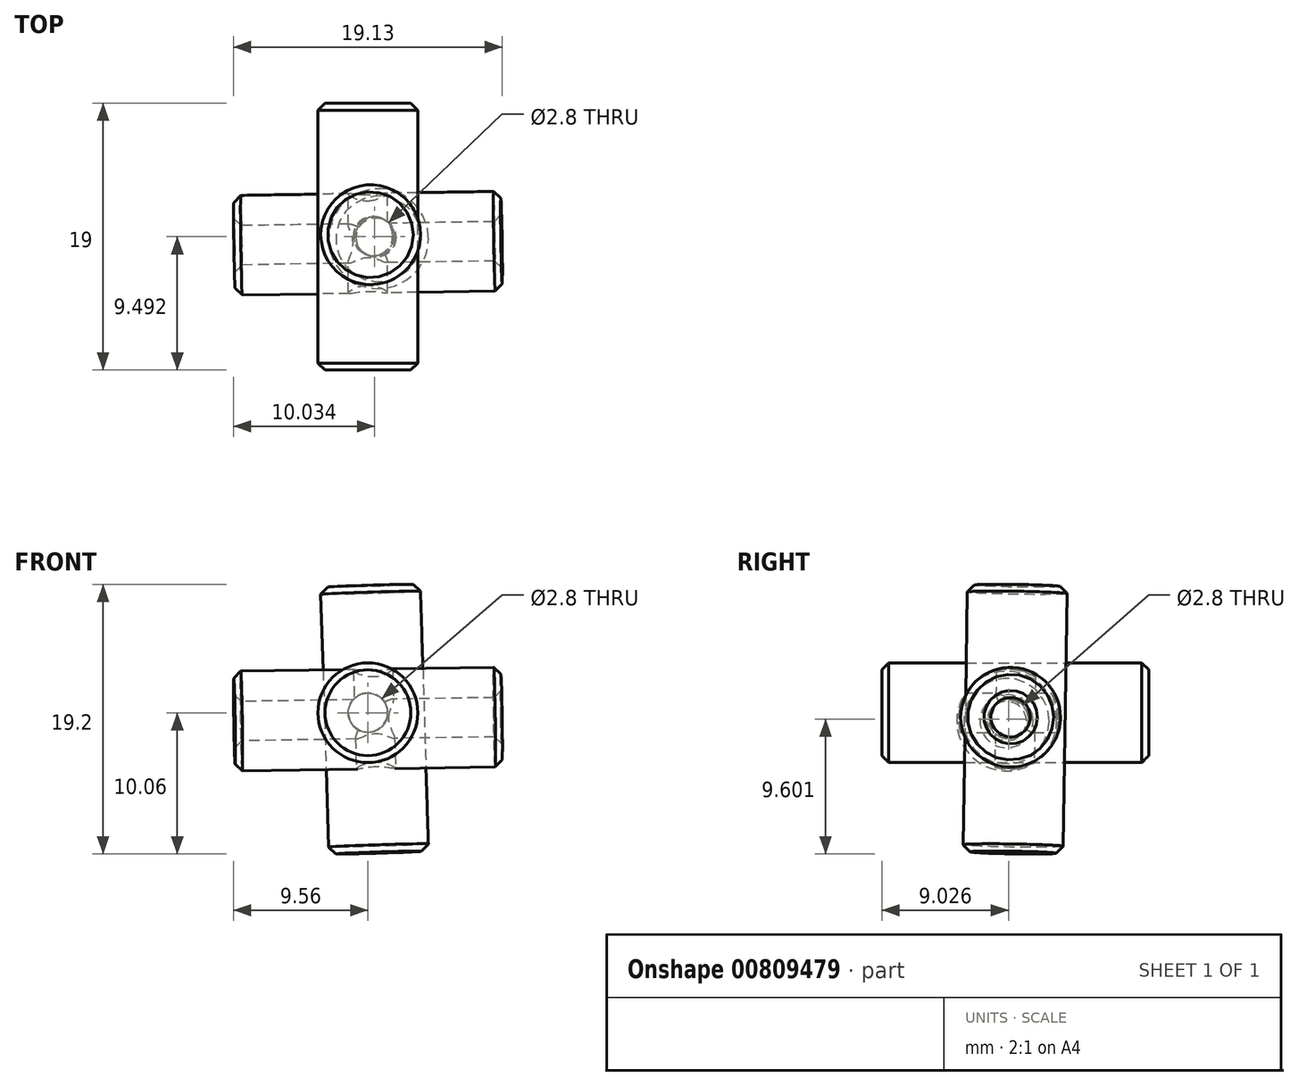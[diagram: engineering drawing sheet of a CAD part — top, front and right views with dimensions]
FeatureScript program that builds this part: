
annotation { "Feature Type Name" : "Feature", "Feature Type Description" : "" }
export const myFeature = defineFeature(function(context is Context, id is Id, definition is map)
    precondition{}
    {
        {
            var Q0;
            Q0=qCreatedBy(makeId("Front.planeOp"),FACE);
            var sketch = newSketch(context, id + "F0", { "sketchPlane" : qUnion([Q0])});
            skCircle(sketch, "E0", {"center": v(0, 0) * mm, "radius": 3.55 * mm});
            skSolve(sketch);
        }
        {
            var Q0;
            Q0=makeQuery(id+"F0.imprint","IMPRINT",FACE,{"disambiguationData":[TD([[makeQuery(id+"F0.imprint","IMPRINT",EDGE,{"derivedFrom":sQuery(id+"F0.wireOp",EDGE,"E0")}),1.0]])]});
            extrude(context, id + "F1", {"entities" : qUnion([Q0]), "endBound" : BoundingType.SYMMETRIC, "depth" : 19 * mm, "offsetDistance" : 25 * mm});
        }
        {
            var Q0;
            Q0=qCreatedBy(makeId("Front.planeOp"),FACE);
            var sketch = newSketch(context, id + "F2", { "sketchPlane" : qUnion([Q0])});
            skCircle(sketch, "E1", {"center": v(0, 0) * mm, "radius": 1.4 * mm});
            skSolve(sketch);
        }
        {
            var Q0;
            Q0 = qSketchRegion(id + "F2", true);
            extrude(context, id + "F3", {"entities" : qUnion([Q0]), "endBound" : BoundingType.SYMMETRIC, "depth" : 20 * mm, "offsetDistance" : 25 * mm});
        }
        {
            var Q0;
            Q0=qCreatedBy(makeId("Front.planeOp"),FACE);
            var sketch = newSketch(context, id + "F4", { "sketchPlane" : qUnion([Q0])});
            skLineSegment(sketch, "E2.bottom", {"start": v(0, 0) * mm, "end": v(10, 0) * mm});
            skLineSegment(sketch, "E2.top", {"start": v(0, 10) * mm, "end": v(10, 10) * mm});
            skLineSegment(sketch, "E2.left", {"start": v(0, 0) * mm, "end": v(0, 10) * mm});
            skLineSegment(sketch, "E2.right", {"start": v(10, 0) * mm, "end": v(10, 10) * mm});
            skSolve(sketch);
        }
        {
            var Q0;
            Q0 = qSketchRegion(id + "F4", true);
            extrude(context, id + "F5", {"entities" : qUnion([Q0]), "depth" : 10 * mm, "offsetDistance" : 25 * mm});
        }
        {
            var Q0;
            Q0=qCreatedBy(makeId("Origin.pointOp"),VERTEX);
            var Q1;
            Q1=makeQuery(id+"F5.opExtrude","CAP_VERTEX",VERTEX,{"disambiguationData":[OSD([sQuery(id+"F4.wireOp",EDGE,"E2.top"),sQuery(id+"F4.wireOp",EDGE,"E2.right")])],"isStart":false});
            var Q2;
            Q2=makeQuery(id+"F5.opExtrude","CAP_VERTEX",VERTEX,{"disambiguationData":[OSD([sQuery(id+"F4.wireOp",EDGE,"E2.bottom"),sQuery(id+"F4.wireOp",EDGE,"E2.right")])],"isStart":false});
            cPlane(context, id + "F6", {"entities" : qUnion([Q0, Q1, Q2]), "cplaneType" : CPlaneType.THREE_POINT, "offset" : 25 * mm, "width" : 150 * mm, "height" : 150 * mm});
        }
        {
            var Q0;
            Q0=qCreatedBy(id+"F6.planeOp",FACE);
            var sketch = newSketch(context, id + "F7", { "sketchPlane" : qUnion([Q0])});
            skLineSegment(sketch, "E3", {"start": v(0, -0.47) * mm, "end": v(14.14, 10) * mm});
            skSolve(sketch);
        }
        {
            var Q0;
            Q0=makeQuery(id+"F5.opExtrude","SWEPT_BODY",BODY,{"disambiguationData":[OSD([sQuery(id+"F4.wireOp",EDGE,"E2.bottom"),sQuery(id+"F4.wireOp",EDGE,"E2.top"),sQuery(id+"F4.wireOp",EDGE,"E2.left"),sQuery(id+"F4.wireOp",EDGE,"E2.right")])]});
            deleteBodies(context, id + "F8", {"entities" : qUnion([Q0])});
        }
        {
            var Q0;
            Q0=makeQuery(id+"F1.opExtrude","SWEPT_BODY",BODY,{"disambiguationData":[OSD([sQuery(id+"F0.wireOp",EDGE,"E0")])]});
            var Q1;
            Q1=makeQuery(id+"F3.opExtrude","SWEPT_BODY",BODY,{"disambiguationData":[OSD([sQuery(id+"F2.wireOp",EDGE,"E1")])]});
            var Q2;
            Q2=sQuery(id+"F7.wireOp",EDGE,"E3");
            circularPattern(context, id + "F9", {"entities" : qUnion([Q0, Q1]), "axis" : qUnion([Q2]), "angle" : 360 * degree, "instanceCount" : 3, "equalSpace" : true});
        }
        {
            var Q0;
            Q0=makeQuery(id+"F9.opPattern","COPY",BODY,{"derivedFrom":makeQuery(id+"F3.opExtrude","SWEPT_BODY",BODY,{"disambiguationData":[OSD([sQuery(id+"F2.wireOp",EDGE,"E1")])]}),"instanceName":"2"});
            var Q1;
            Q1=makeQuery(id+"F3.opExtrude","SWEPT_BODY",BODY,{"disambiguationData":[OSD([sQuery(id+"F2.wireOp",EDGE,"E1")])]});
            var Q2;
            Q2=makeQuery(id+"F9.opPattern","COPY",BODY,{"derivedFrom":makeQuery(id+"F3.opExtrude","SWEPT_BODY",BODY,{"disambiguationData":[OSD([sQuery(id+"F2.wireOp",EDGE,"E1")])]}),"instanceName":"1"});
            var Q3;
            Q3=makeQuery(id+"F9.opPattern","COPY",BODY,{"derivedFrom":makeQuery(id+"F1.opExtrude","SWEPT_BODY",BODY,{"disambiguationData":[OSD([sQuery(id+"F0.wireOp",EDGE,"E0")])]}),"instanceName":"1"});
            booleanBodies(context, id + "F10", {"operationType" : BooleanOperationType.SUBTRACTION, "tools" : qUnion([Q0, Q1, Q2]), "targets" : qUnion([Q3])});
        }
        {
            var Q0;
            Q0=makeQuery(id+"F1.opExtrude","CAP_FACE",FACE,{"disambiguationData":[OSD([sQuery(id+"F0.wireOp",EDGE,"E0")])],"isStart":false});
            var Q1;
            Q1=makeQuery(id+"F9.opPattern","COPY",FACE,{"derivedFrom":makeQuery(id+"F1.opExtrude","CAP_FACE",FACE,{"disambiguationData":[OSD([sQuery(id+"F0.wireOp",EDGE,"E0")])],"isStart":true}),"instanceName":"2"});
            var Q2;
            Q2=makeQuery(id+"F1.opExtrude","CAP_FACE",FACE,{"disambiguationData":[OSD([sQuery(id+"F0.wireOp",EDGE,"E0")])],"isStart":true});
            var Q3;
            Q3=makeQuery(id+"F9.opPattern","COPY",FACE,{"derivedFrom":makeQuery(id+"F1.opExtrude","CAP_FACE",FACE,{"disambiguationData":[OSD([sQuery(id+"F0.wireOp",EDGE,"E0")])],"isStart":false}),"instanceName":"1"});
            var Q4;
            Q4=makeQuery(id+"F9.opPattern","COPY",FACE,{"derivedFrom":makeQuery(id+"F1.opExtrude","CAP_FACE",FACE,{"disambiguationData":[OSD([sQuery(id+"F0.wireOp",EDGE,"E0")])],"isStart":true}),"instanceName":"1"});
            var Q5;
            Q5=makeQuery(id+"F9.opPattern","COPY",FACE,{"derivedFrom":makeQuery(id+"F1.opExtrude","CAP_FACE",FACE,{"disambiguationData":[OSD([sQuery(id+"F0.wireOp",EDGE,"E0")])],"isStart":false}),"instanceName":"2"});
            chamfer(context, id + "F11", {"entities" : qUnion([Q0, Q1, Q2, Q3, Q4, Q5]), "width" : 0.5 * mm, "tangentPropagation" : true});
        }
    });
